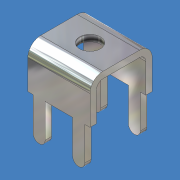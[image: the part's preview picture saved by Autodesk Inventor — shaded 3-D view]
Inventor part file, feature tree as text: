
AUTODESK INVENTOR PART (.ipt)
format: ipt  version: 2014 SP1 (Build 180222100, 222)  size: 200,192 bytes
history: native  units: mm (DEFAULTED — no unit token found)
features: sheet_metal_op x13, sketch x8, other x7, hole x1, chamfer x1
ambient origin geometry x8: Origin, YZ Plane, XZ Plane, XY Plane, X Axis, Y Axis, Z Axis, Center Point
bodies: Solid1 (feature_tree)
feature tree (30):
  sheet_metal_op  "Face1"
  sheet_metal_op  "Flange1"
  sheet_metal_op  "Flange2"
  hole  "Hole1"  [1 undecoded]
  sheet_metal_op  "Flange3"
  sheet_metal_op  "Flange4"
  sheet_metal_op  "Flange5"
  sheet_metal_op  "Flange6"
  chamfer  "Corner Round1"
  sketch  "Sketch1"  dims[d0=7.874mm d1=7.874mm]
  other  "Plate1"
  sketch  "Sketch2"  dims[d2=0.8128mm]
  other  "Plate2"
  sheet_metal_op  "Bend1"
  sketch  "Sketch3"  dims[d3=0.8128mm]
  other  "Plate3"
  sheet_metal_op  "Bend2"
  sketch  "Sketch4"  dims[d4=5.334mm d5=90.0deg d6=0.8128mm]
  sketch  "Sketch5"  dims[d7=0.8128mm]
  other  "Plate4"
  sheet_metal_op  "Bend3"
  sketch  "Sketch6"  dims[d8=5.334mm d9=90.0deg d10=0.8128mm]
  other  "Plate5"
  sheet_metal_op  "Bend4"
  sketch  "Sketch7"  dims[d11=2.6416mm d12=12.7mm d13=9.525mm d14=6.35mm d15=14.3117mm d16=19.05mm d17=20.594885mm]
  other  "Plate6"
  sheet_metal_op  "Bend5"
  sketch  "Sketch8"  dims[d18=0.6731mm d19=1.524mm d20=0.8128mm d21=5.0038mm d22=0.0mm d23=0.8128mm d25=0.6731mm d26=1.524mm d27=0.8128mm d28=5.0038mm d29=0.0mm d30=0.8128mm d31=0.6731mm d32=1.524mm d33=0.8128mm d34=5.0038mm d35=0.0mm d36=0.8128mm d37=0.6731mm d38=1.524mm d39=0.8128mm d40=5.0038mm d41=0.0mm d42=0.8128mm d43=0.762mm d44=0.8128mm d45=0.4064mm d46=1.6256mm d47=0.8128mm d48=0.4064mm d49=1.6256mm d50=0.8128mm d51=0.4064mm d52=1.6256mm d53=0.8128mm d54=0.4064mm d55=1.6256mm d56=0.8128mm d57=0.4064mm d58=1.6256mm d59=0.8128mm d60=0.4064mm d61=1.6256mm]
  other  "Plate7"
  sheet_metal_op  "Bend6"
note: 1 required parameter value undecoded (feature->parameter linkage not recoverable at this tier; creation-order binding heuristic only, values carry confidence <= 0.55)
